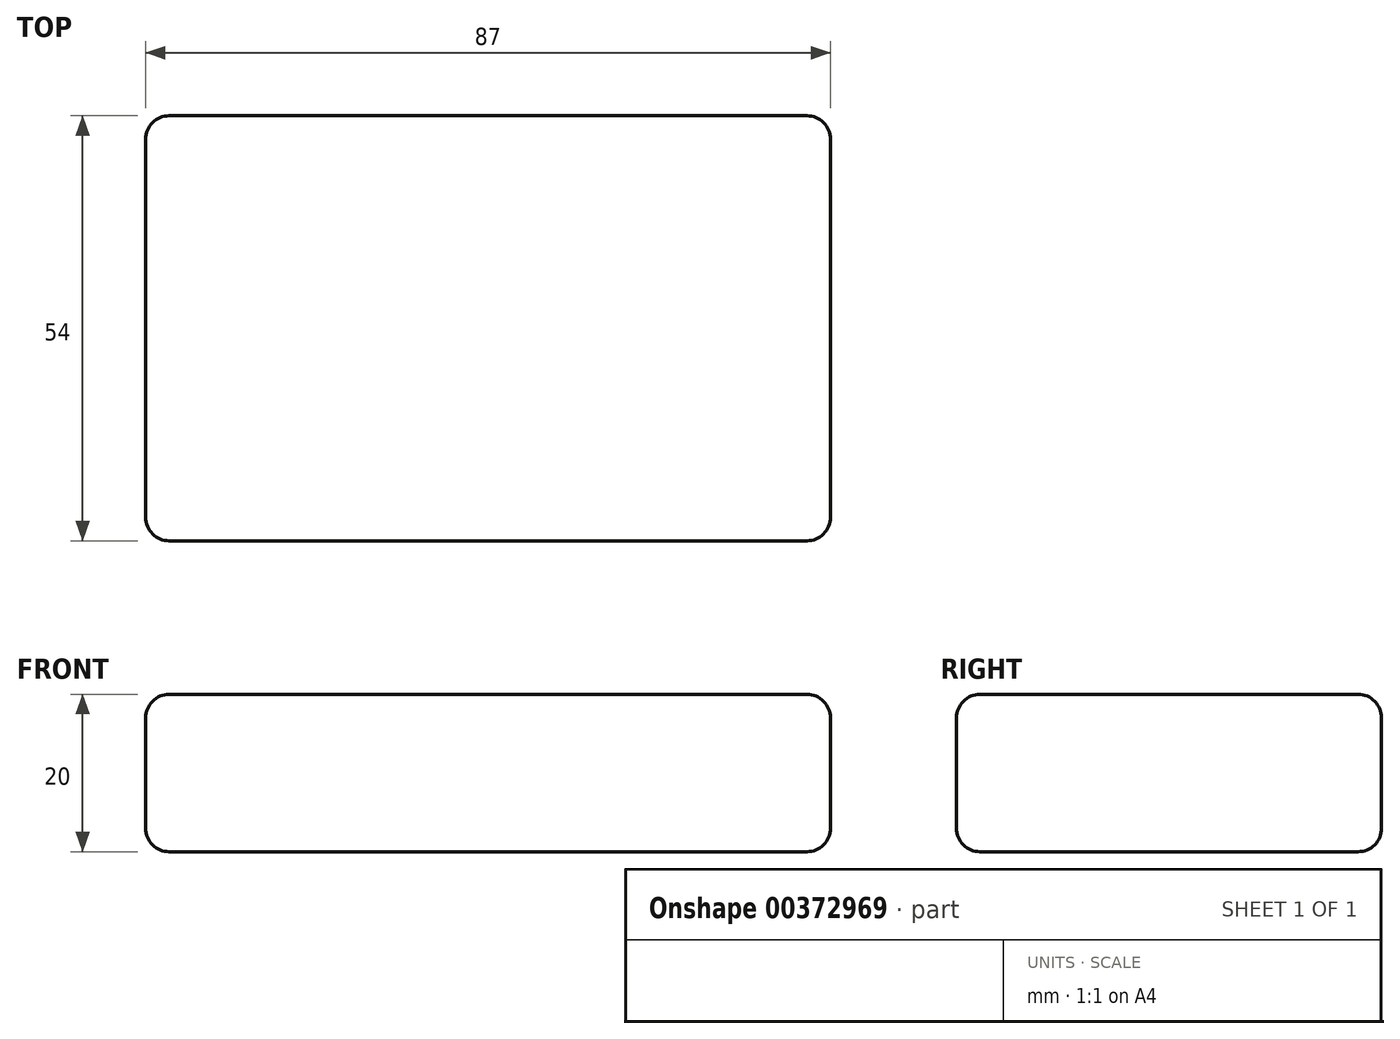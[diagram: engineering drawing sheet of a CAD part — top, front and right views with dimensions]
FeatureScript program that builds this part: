
annotation { "Feature Type Name" : "Feature", "Feature Type Description" : "" }
export const myFeature = defineFeature(function(context is Context, id is Id, definition is map)
    precondition{}
    {
        {
            var Q0;
            Q0=qCreatedBy(makeId("Top.planeOp"),FACE);
            var sketch = newSketch(context, id + "F0", { "sketchPlane" : qUnion([Q0])});
            skLineSegment(sketch, "E0.bottom", {"start": v(43.5, 27) * mm, "end": v(-43.5, 27) * mm});
            skLineSegment(sketch, "E0.top", {"start": v(43.5, -27) * mm, "end": v(-43.5, -27) * mm});
            skLineSegment(sketch, "E0.left", {"start": v(43.5, 27) * mm, "end": v(43.5, -27) * mm});
            skLineSegment(sketch, "E0.right", {"start": v(-43.5, 27) * mm, "end": v(-43.5, -27) * mm});
            skPoint(sketch, "E0.middle", {"position": v(0, 0) * mm});
            skSolve(sketch);
        }
        {
            var Q0;
            Q0=makeQuery(id+"F0.imprint","IMPRINT",FACE,{"disambiguationData":[TD([[makeQuery(id+"F0.imprint","IMPRINT",EDGE,{"derivedFrom":sQuery(id+"F0.wireOp",EDGE,"E0.bottom")}),1.0]])]});
            extrude(context, id + "F1", {"entities" : qUnion([Q0]), "depth" : 20 * mm});
        }
        {
            var Q0;
            Q0=makeQuery(id+"F1.opExtrude","CAP_FACE",FACE,{"disambiguationData":[OSD([sQuery(id+"F0.wireOp",EDGE,"E0.bottom"),sQuery(id+"F0.wireOp",EDGE,"E0.top"),sQuery(id+"F0.wireOp",EDGE,"E0.left"),sQuery(id+"F0.wireOp",EDGE,"E0.right")])],"isStart":false});
            var Q1;
            Q1=makeQuery(id+"F1.opExtrude","CAP_FACE",FACE,{"disambiguationData":[OSD([sQuery(id+"F0.wireOp",EDGE,"E0.bottom"),sQuery(id+"F0.wireOp",EDGE,"E0.top"),sQuery(id+"F0.wireOp",EDGE,"E0.left"),sQuery(id+"F0.wireOp",EDGE,"E0.right")])],"isStart":true});
            var Q2;
            Q2=makeQuery(id+"F1.opExtrude","SWEPT_EDGE",EDGE,{"disambiguationData":[OSD([sQuery(id+"F0.wireOp",EDGE,"E0.top"),sQuery(id+"F0.wireOp",EDGE,"E0.right")])]});
            var Q3;
            Q3=makeQuery(id+"F1.opExtrude","SWEPT_EDGE",EDGE,{"disambiguationData":[OSD([sQuery(id+"F0.wireOp",EDGE,"E0.top"),sQuery(id+"F0.wireOp",EDGE,"E0.left")])]});
            var Q4;
            Q4=makeQuery(id+"F1.opExtrude","SWEPT_EDGE",EDGE,{"disambiguationData":[OSD([sQuery(id+"F0.wireOp",EDGE,"E0.bottom"),sQuery(id+"F0.wireOp",EDGE,"E0.right")])]});
            var Q5;
            Q5=makeQuery(id+"F1.opExtrude","SWEPT_EDGE",EDGE,{"disambiguationData":[OSD([sQuery(id+"F0.wireOp",EDGE,"E0.bottom"),sQuery(id+"F0.wireOp",EDGE,"E0.left")])]});
            fillet(context, id + "F2", {"entities" : qUnion([Q0, Q1, Q2, Q3, Q4, Q5]), "radius" : 3 * mm, "tangentPropagation" : true, "allowEdgeOverflow" : false});
        }
    });
